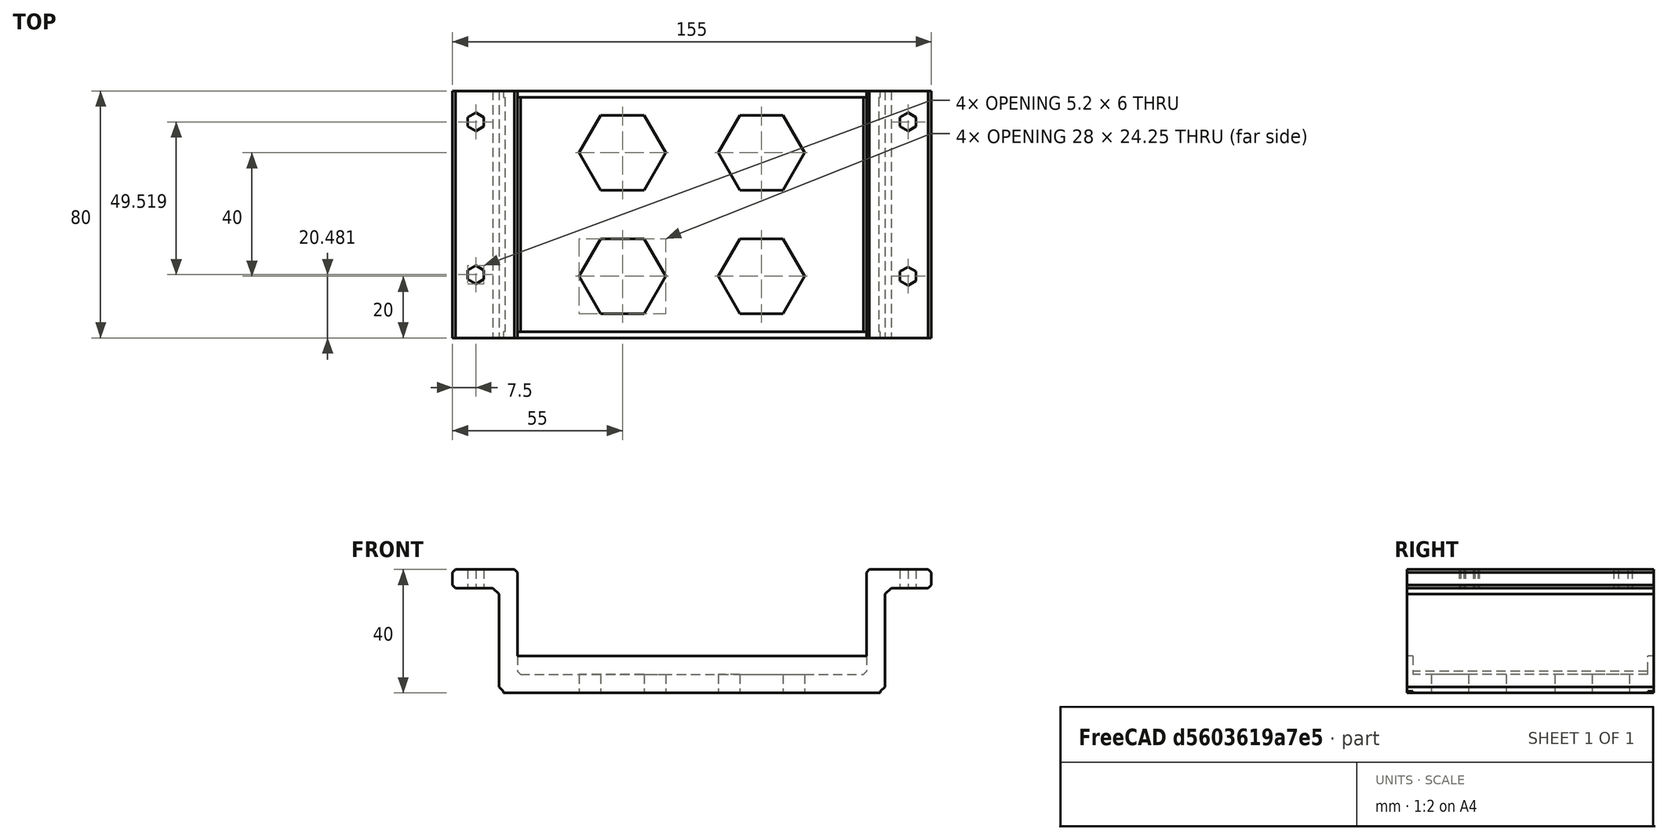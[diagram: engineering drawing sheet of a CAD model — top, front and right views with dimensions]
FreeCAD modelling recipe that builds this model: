
FCSTD DOCUMENT  (FreeCAD 0.19R)
Label: GaNprime
License: All rights reserved
LicenseURL: http://en.wikipedia.org/wiki/All_rights_reserved
objects: Sketcher::SketchObject×4, PartDesign::Chamfer×4, PartDesign::Pad×2, PartDesign::Pocket×2, PartDesign::Body×1, Mesh::Feature×1
note: 21 computed .brp shape members not serialized (recipe doc carries the construction recipe); baked Part::Feature solids carry a one-line shape summary decoded from their .brp

FEATURE [Sketcher::SketchObject] Sketch
  FullyConstrained = true
  MapMode = 5
  Placement = pos=(0,0,0) rot=(1,0,0;1.5708rad)
  Support = -> [XZ_Plane]
  sketch-geometry (12):
    g0: LineSegment StartX=-77.5 StartY=0 StartZ=0 EndX=-77.5 EndY=-6 EndZ=0
    g1: LineSegment StartX=-77.5 StartY=-6 StartZ=0 EndX=-62.5 EndY=-6 EndZ=0
    g2: LineSegment StartX=-62.5 StartY=-6 StartZ=0 EndX=-62.5 EndY=-40 EndZ=0
    g3: LineSegment StartX=-62.5 StartY=-40 StartZ=0 EndX=62.5 EndY=-40 EndZ=0
    g4: LineSegment StartX=62.5 StartY=-40 StartZ=0 EndX=62.5 EndY=-6 EndZ=0
    g5: LineSegment StartX=62.5 StartY=-6 StartZ=0 EndX=77.5 EndY=-6 EndZ=0
    g6: LineSegment StartX=77.5 StartY=-6 StartZ=0 EndX=77.5 EndY=0 EndZ=0
    g7: LineSegment StartX=77.5 StartY=0 StartZ=0 EndX=56.5 EndY=0 EndZ=0
    g8: LineSegment StartX=56.5 StartY=0 StartZ=0 EndX=56.5 EndY=-34 EndZ=0
    g9: LineSegment StartX=56.5 StartY=-34 StartZ=0 EndX=-56.5 EndY=-34 EndZ=0
    g10: LineSegment StartX=-56.5 StartY=-34 StartZ=0 EndX=-56.5 EndY=0 EndZ=0
    g11: LineSegment StartX=-56.5 StartY=0 StartZ=0 EndX=-77.5 EndY=0 EndZ=0
  constraints (34):
    c: PointOnObject(g0,g-1)
    c: Vertical(g0)
    c: Coincident(g0,g1)
    c: Horizontal(g1)
    c: Coincident(g1,g2)
    c: Vertical(g2)
    c: Coincident(g2,g3)
    c: Horizontal(g3)
    c: Coincident(g3,g4)
    c: Coincident(g4,g5)
    c: Coincident(g5,g6)
    c: PointOnObject(g6,g-1)
    c: Coincident(g6,g7)
    c: PointOnObject(g7,g-1)
    c: Coincident(g7,g8)
    c: Vertical(g8)
    c: Coincident(g8,g9)
    c: Coincident(g9,g10)
    c: Coincident(g10,g11)
    c: Coincident(g11,g0)
    c: Symmetric(g7,g10,g-2)
    c: Vertical(g10)
    c: Horizontal(g9)
    c: Equal(g7,g11)
    c: Equal(g6,g0)
    c: Vertical(g6)
    c: Symmetric(g4,g1,g-2)
    c: Vertical(g4)
    c: Distance(g9) = 113
    c: Distance(g4,g8) = 6
    c: Distance(g3,g9) = 6
    c: Distance(g8) = 34
    c: Distance(g0) = 6
    c: Distance(g1) = 15
FEATURE [PartDesign::Pad] Pad
  Direction = (1,1,1)
  Length = 80
  Length2 = 100
  Placement = pos=(0,0,0) rot=(1,0,0;1.5708rad)
  Profile = -> Sketch
  Type = 0
FEATURE [Sketcher::SketchObject] Sketch001
  FullyConstrained = false
  MapMode = 5
  Placement = pos=(0,0,0) rot=(0,0,1;3.14159rad)
  Support = -> [Pad]
  sketch-geometry (28):
    g0: LineSegment StartX=-70 StartY=7 StartZ=0 EndX=-67.4019 EndY=8.5 EndZ=0
    g1: LineSegment StartX=-67.4019 StartY=8.5 StartZ=0 EndX=-67.4019 EndY=11.5 EndZ=0
    g2: LineSegment StartX=-67.4019 StartY=11.5 StartZ=0 EndX=-70 EndY=13 EndZ=0
    g3: LineSegment StartX=-70 StartY=13 StartZ=0 EndX=-72.5981 EndY=11.5 EndZ=0
    g4: LineSegment StartX=-72.5981 StartY=11.5 StartZ=0 EndX=-72.5981 EndY=8.5 EndZ=0
    g5: LineSegment StartX=-72.5981 StartY=8.5 StartZ=0 EndX=-70 EndY=7 EndZ=0
    g6: Circle CenterX=-70 CenterY=10 CenterZ=0 NormalX=0 NormalY=0 NormalZ=1 AngleXU=0 Radius=3
    g7: LineSegment StartX=70 StartY=56.5194 StartZ=0 EndX=72.5981 EndY=58.0194 EndZ=0
    g8: LineSegment StartX=72.5981 StartY=58.0194 StartZ=0 EndX=72.5981 EndY=61.0194 EndZ=0
    g9: LineSegment StartX=72.5981 StartY=61.0194 StartZ=0 EndX=70 EndY=62.5194 EndZ=0
    g10: LineSegment StartX=70 StartY=62.5194 StartZ=0 EndX=67.4019 EndY=61.0194 EndZ=0
    g11: LineSegment StartX=67.4019 StartY=61.0194 StartZ=0 EndX=67.4019 EndY=58.0194 EndZ=0
    g12: LineSegment StartX=67.4019 StartY=58.0194 StartZ=0 EndX=70 EndY=56.5194 EndZ=0
    g13: Circle CenterX=70 CenterY=59.5194 CenterZ=0 NormalX=0 NormalY=0 NormalZ=1 AngleXU=0 Radius=3
    g14: LineSegment StartX=70 StartY=7 StartZ=0 EndX=72.5981 EndY=8.5 EndZ=0
    g15: LineSegment StartX=72.5981 StartY=8.5 StartZ=0 EndX=72.5981 EndY=11.5 EndZ=0
    g16: LineSegment StartX=72.5981 StartY=11.5 StartZ=0 EndX=70 EndY=13 EndZ=0
    g17: LineSegment StartX=70 StartY=13 StartZ=0 EndX=67.4019 EndY=11.5 EndZ=0
    g18: LineSegment StartX=67.4019 StartY=11.5 StartZ=0 EndX=67.4019 EndY=8.5 EndZ=0
    g19: LineSegment StartX=67.4019 StartY=8.5 StartZ=0 EndX=70 EndY=7 EndZ=0
    g20: Circle CenterX=70 CenterY=10 CenterZ=0 NormalX=0 NormalY=0 NormalZ=1 AngleXU=0 Radius=3
    g21: LineSegment StartX=-70 StartY=57 StartZ=0 EndX=-67.4019 EndY=58.5 EndZ=0
    g22: LineSegment StartX=-67.4019 StartY=58.5 StartZ=0 EndX=-67.4019 EndY=61.5 EndZ=0
    g23: LineSegment StartX=-67.4019 StartY=61.5 StartZ=0 EndX=-70 EndY=63 EndZ=0
    g24: LineSegment StartX=-70 StartY=63 StartZ=0 EndX=-72.5981 EndY=61.5 EndZ=0
    g25: LineSegment StartX=-72.5981 StartY=61.5 StartZ=0 EndX=-72.5981 EndY=58.5 EndZ=0
    g26: LineSegment StartX=-72.5981 StartY=58.5 StartZ=0 EndX=-70 EndY=57 EndZ=0
    g27: Circle CenterX=-70 CenterY=60 CenterZ=0 NormalX=0 NormalY=0 NormalZ=1 AngleXU=0 Radius=3
  constraints (66):
    c: Coincident(g0,g1)
    c: Coincident(g1,g2)
    c: Coincident(g2,g3)
    c: Coincident(g3,g4)
    c: Coincident(g4,g5)
    c: Coincident(g5,g0)
    c: Equal(g0, g1-g5) x5
    c: PointOnObject(g0,g6)
    c: PointOnObject(g1,g6)
    c: PointOnObject(g2,g6)
    c: PointOnObject(g3,g6)
    c: PointOnObject(g4,g6)
    c: PointOnObject(g5,g6)
    c: Coincident(g7,g8)
    c: Coincident(g8,g9)
    c: Coincident(g9,g10)
    c: Coincident(g10,g11)
    c: Coincident(g11,g12)
    c: Coincident(g12,g7)
    c: Equal(g7, g8-g12) x5
    c: PointOnObject(g7,g13)
    c: PointOnObject(g8,g13)
    c: PointOnObject(g9,g13)
    c: PointOnObject(g10,g13)
    c: PointOnObject(g11,g13)
    c: PointOnObject(g12,g13)
    c: Coincident(g14,g15)
    c: Coincident(g15,g16)
    c: Coincident(g16,g17)
    c: Coincident(g17,g18)
    c: Coincident(g18,g19)
    c: Coincident(g19,g14)
    c: Equal(g14, g15-g19) x5
    c: PointOnObject(g14,g20)
    c: PointOnObject(g15,g20)
    c: PointOnObject(g16,g20)
    c: PointOnObject(g17,g20)
    c: PointOnObject(g18,g20)
    c: PointOnObject(g19,g20)
    c: Vertical(g1)
    c: Vertical(g8)
    c: Vertical(g15)
    c: Symmetric(g6,g20,g-2)
    c: DistanceY(g6) = 10
    c: Coincident(g21,g22)
    c: Coincident(g22,g23)
    c: Coincident(g23,g24)
    c: Coincident(g24,g25)
    c: Coincident(g25,g26)
    c: Coincident(g26,g21)
    c: Equal(g21, g22-g26) x5
    c: PointOnObject(g21,g27)
    c: PointOnObject(g22,g27)
    c: PointOnObject(g23,g27)
    c: PointOnObject(g24,g27)
    c: PointOnObject(g25,g27)
    c: PointOnObject(g26,g27)
    c: Diameter(g27) = 6
    c: Vertical(g22)
    c: DistanceY(g27) = 60
    c: Diameter(g13) = 6
    c: Equal(g13,g20)
    c: Equal(g13,g6)
    c: Distance(g6,g20) = 140
    c: DistanceX(g13,g20) = 0
    c: DistanceX(g6,g27) = 0
FEATURE [PartDesign::Pocket] Pocket
  BaseFeature = -> Pad
  Length = 5
  Length2 = 100
  Placement = pos=(0,0,0) rot=(1,0,0;1.5708rad)
  Profile = -> Sketch001
  Type = 1
FEATURE [PartDesign::Chamfer] Chamfer
  Angle = 45
  Base = -> Pocket [Edge53,Edge96]
  BaseFeature = -> Pocket
  ChamferType = 0
  FlipDirection = false
  Placement = pos=(0,0,0) rot=(1,0,0;1.5708rad)
  Size = 1
  Size2 = 1
  SupportTransform = false
FEATURE [PartDesign::Chamfer] Chamfer001
  Angle = 45
  Base = -> Chamfer [Edge72,Edge56]
  BaseFeature = -> Chamfer
  ChamferType = 0
  FlipDirection = false
  Placement = pos=(0,0,0) rot=(1,0,0;1.5708rad)
  Size = 2
  Size2 = 1
  SupportTransform = false
FEATURE [PartDesign::Chamfer] Chamfer002
  Angle = 45
  Base = -> Chamfer001 [Edge23,Edge60,Edge38,Edge43,Edge80,Edge76]
  BaseFeature = -> Chamfer001
  ChamferType = 0
  FlipDirection = false
  Placement = pos=(0,0,0) rot=(1,0,0;1.5708rad)
  Size = 1
  Size2 = 1
  SupportTransform = false
FEATURE [PartDesign::Chamfer] Chamfer003
  Angle = 45
  Base = -> Chamfer002 [Edge68,Edge24]
  BaseFeature = -> Chamfer002
  ChamferType = 0
  FlipDirection = false
  Placement = pos=(0,0,0) rot=(1,0,0;1.5708rad)
  Size = 2
  Size2 = 1
  SupportTransform = false
FEATURE [Sketcher::SketchObject] Sketch002
  FullyConstrained = true
  MapMode = 5
  Placement = pos=(0,-4.44e-14,-40) rot=(1,0,0;3.14159rad)
  Support = -> [Chamfer003]
  sketch-geometry (8):
    g0: LineSegment StartX=-61 StartY=80 StartZ=0 EndX=61 EndY=80 EndZ=0
    g1: LineSegment StartX=61 StartY=80 StartZ=0 EndX=61 EndY=78 EndZ=0
    g2: LineSegment StartX=61 StartY=78 StartZ=0 EndX=-61 EndY=78 EndZ=0
    g3: LineSegment StartX=-61 StartY=78 StartZ=0 EndX=-61 EndY=80 EndZ=0
    g4: LineSegment StartX=-61 StartY=2 StartZ=0 EndX=61 EndY=2 EndZ=0
    g5: LineSegment StartX=61 StartY=2 StartZ=0 EndX=61 EndY=0 EndZ=0
    g6: LineSegment StartX=61 StartY=0 StartZ=0 EndX=-61 EndY=0 EndZ=0
    g7: LineSegment StartX=-61 StartY=0 StartZ=0 EndX=-61 EndY=2 EndZ=0
  constraints (22):
    c: Coincident(g0,g1)
    c: Coincident(g1,g2)
    c: Coincident(g2,g3)
    c: Coincident(g3,g0)
    c: Horizontal(g2)
    c: Vertical(g1)
    c: Vertical(g3)
    c: Coincident(g4,g5)
    c: Coincident(g5,g6)
    c: Coincident(g6,g7)
    c: Coincident(g7,g4)
    c: Horizontal(g6)
    c: Vertical(g5)
    c: Vertical(g7)
    c: Distance(g5) = 2
    c: Distance(g1) = 2
    c: PointOnObject(g5,g-1)
    c: DistanceY(g0) = 80
    c: Symmetric(g0,g0,g-2)
    c: Distance(g0) = 122
    c: Equal(g4,g2)
    c: Symmetric(g4,g4,g-2)
FEATURE [PartDesign::Pad] Pad001
  BaseFeature = -> Chamfer003
  Direction = (1,1,1)
  Length = 12
  Length2 = 100
  Placement = pos=(0,0,0) rot=(1,0,0;1.5708rad)
  Profile = -> Sketch002
  Reversed = true
  Type = 0
FEATURE [Sketcher::SketchObject] Sketch003
  FullyConstrained = true
  MapMode = 5
  Placement = pos=(0,-5.28e-14,-34) rot=(0,0,1;3.14159rad)
  Support = -> [Pad001]
  sketch-geometry (28):
    g0: LineSegment StartX=-15.5 StartY=47.8756 StartZ=0 EndX=-8.5 EndY=60 EndZ=0
    g1: LineSegment StartX=-8.5 StartY=60 StartZ=0 EndX=-15.5 EndY=72.1244 EndZ=0
    g2: LineSegment StartX=-15.5 StartY=72.1244 StartZ=0 EndX=-29.5 EndY=72.1244 EndZ=0
    g3: LineSegment StartX=-29.5 StartY=72.1244 StartZ=0 EndX=-36.5 EndY=60 EndZ=0
    g4: LineSegment StartX=-36.5 StartY=60 StartZ=0 EndX=-29.5 EndY=47.8756 EndZ=0
    g5: LineSegment StartX=-29.5 StartY=47.8756 StartZ=0 EndX=-15.5 EndY=47.8756 EndZ=0
    g6: Circle CenterX=-22.5 CenterY=60 CenterZ=0 NormalX=0 NormalY=0 NormalZ=1 AngleXU=0 Radius=14
    g7: LineSegment StartX=-15.5 StartY=7.87564 StartZ=0 EndX=-8.5 EndY=20 EndZ=0
    g8: LineSegment StartX=-8.5 StartY=20 StartZ=0 EndX=-15.5 EndY=32.1244 EndZ=0
    g9: LineSegment StartX=-15.5 StartY=32.1244 StartZ=0 EndX=-29.5 EndY=32.1244 EndZ=0
    g10: LineSegment StartX=-29.5 StartY=32.1244 StartZ=0 EndX=-36.5 EndY=20 EndZ=0
    g11: LineSegment StartX=-36.5 StartY=20 StartZ=0 EndX=-29.5 EndY=7.87564 EndZ=0
    g12: LineSegment StartX=-29.5 StartY=7.87564 StartZ=0 EndX=-15.5 EndY=7.87564 EndZ=0
    g13: Circle CenterX=-22.5 CenterY=20 CenterZ=0 NormalX=0 NormalY=0 NormalZ=1 AngleXU=0 Radius=14
    g14: LineSegment StartX=15.5 StartY=47.8756 StartZ=0 EndX=29.5 EndY=47.8756 EndZ=0
    g15: LineSegment StartX=29.5 StartY=47.8756 StartZ=0 EndX=36.5 EndY=60 EndZ=0
    g16: LineSegment StartX=36.5 StartY=60 StartZ=0 EndX=29.5 EndY=72.1244 EndZ=0
    g17: LineSegment StartX=29.5 StartY=72.1244 StartZ=0 EndX=15.5 EndY=72.1244 EndZ=0
    g18: LineSegment StartX=15.5 StartY=72.1244 StartZ=0 EndX=8.5 EndY=60 EndZ=0
    g19: LineSegment StartX=8.5 StartY=60 StartZ=0 EndX=15.5 EndY=47.8756 EndZ=0
    g20: Circle CenterX=22.5 CenterY=60 CenterZ=0 NormalX=0 NormalY=0 NormalZ=1 AngleXU=0 Radius=14
    g21: LineSegment StartX=15.5 StartY=7.87564 StartZ=0 EndX=29.5 EndY=7.87564 EndZ=0
    g22: LineSegment StartX=29.5 StartY=7.87564 StartZ=0 EndX=36.5 EndY=20 EndZ=0
    g23: LineSegment StartX=36.5 StartY=20 StartZ=0 EndX=29.5 EndY=32.1244 EndZ=0
    g24: LineSegment StartX=29.5 StartY=32.1244 StartZ=0 EndX=15.5 EndY=32.1244 EndZ=0
    g25: LineSegment StartX=15.5 StartY=32.1244 StartZ=0 EndX=8.5 EndY=20 EndZ=0
    g26: LineSegment StartX=8.5 StartY=20 StartZ=0 EndX=15.5 EndY=7.87564 EndZ=0
    g27: Circle CenterX=22.5 CenterY=20 CenterZ=0 NormalX=0 NormalY=0 NormalZ=1 AngleXU=0 Radius=14
  constraints (66):
    c: Coincident(g0,g1)
    c: Coincident(g1,g2)
    c: Coincident(g2,g3)
    c: Coincident(g3,g4)
    c: Coincident(g4,g5)
    c: Coincident(g5,g0)
    c: Equal(g0, g1-g5) x5
    c: PointOnObject(g0,g6)
    c: PointOnObject(g1,g6)
    c: PointOnObject(g2,g6)
    c: PointOnObject(g3,g6)
    c: PointOnObject(g4,g6)
    c: PointOnObject(g5,g6)
    c: Coincident(g7,g8)
    c: Coincident(g8,g9)
    c: Coincident(g9,g10)
    c: Coincident(g10,g11)
    c: Coincident(g11,g12)
    c: Coincident(g12,g7)
    c: Equal(g7, g8-g12) x5
    c: PointOnObject(g7,g13)
    c: PointOnObject(g8,g13)
    c: PointOnObject(g9,g13)
    c: PointOnObject(g10,g13)
    c: PointOnObject(g11,g13)
    c: PointOnObject(g12,g13)
    c: Coincident(g14,g15)
    c: Coincident(g15,g16)
    c: Coincident(g16,g17)
    c: Coincident(g17,g18)
    c: Coincident(g18,g19)
    c: Coincident(g19,g14)
    c: Equal(g14, g15-g19) x5
    c: PointOnObject(g14,g20)
    c: PointOnObject(g15,g20)
    c: PointOnObject(g16,g20)
    c: PointOnObject(g17,g20)
    c: PointOnObject(g18,g20)
    c: PointOnObject(g19,g20)
    c: Coincident(g21,g22)
    c: Coincident(g22,g23)
    c: Coincident(g23,g24)
    c: Coincident(g24,g25)
    c: Coincident(g25,g26)
    c: Coincident(g26,g21)
    c: Equal(g21, g22-g26) x5
    c: PointOnObject(g21,g27)
    c: PointOnObject(g22,g27)
    c: PointOnObject(g23,g27)
    c: PointOnObject(g24,g27)
    c: PointOnObject(g25,g27)
    c: PointOnObject(g26,g27)
    c: Diameter(g6) = 28
    c: Equal(g6,g13)
    c: Equal(g6,g27)
    c: Equal(g6,g20)
    c: Symmetric(g13,g27,g-2)
    c: Symmetric(g20,g6,g-2)
    c: Distance(g13,g27) = 45
    c: DistanceX(g6,g13) = 0
    c: DistanceY(g27) = 20
    c: DistanceY(g20) = 60
    c: Horizontal(g5)
    c: Horizontal(g14)
    c: Horizontal(g12)
    c: Horizontal(g21)
FEATURE [PartDesign::Pocket] Pocket001
  BaseFeature = -> Pad001
  Length = 15
  Length2 = 100
  Placement = pos=(0,0,0) rot=(1,0,0;1.5708rad)
  Profile = -> Sketch003
  Type = 0
FEATURE [PartDesign::Body] Body
  Group = -> [Sketch,Pad,Sketch001,Pocket,Chamfer,Chamfer001,Chamfer002,Chamfer003,Sketch002,Pad001,Sketch003,Pocket001]
  Origin = -> Origin
  Tip = -> Pocket001
FEATURE [Mesh::Feature] Mesh  label="Pocket001 (Meshed)"
